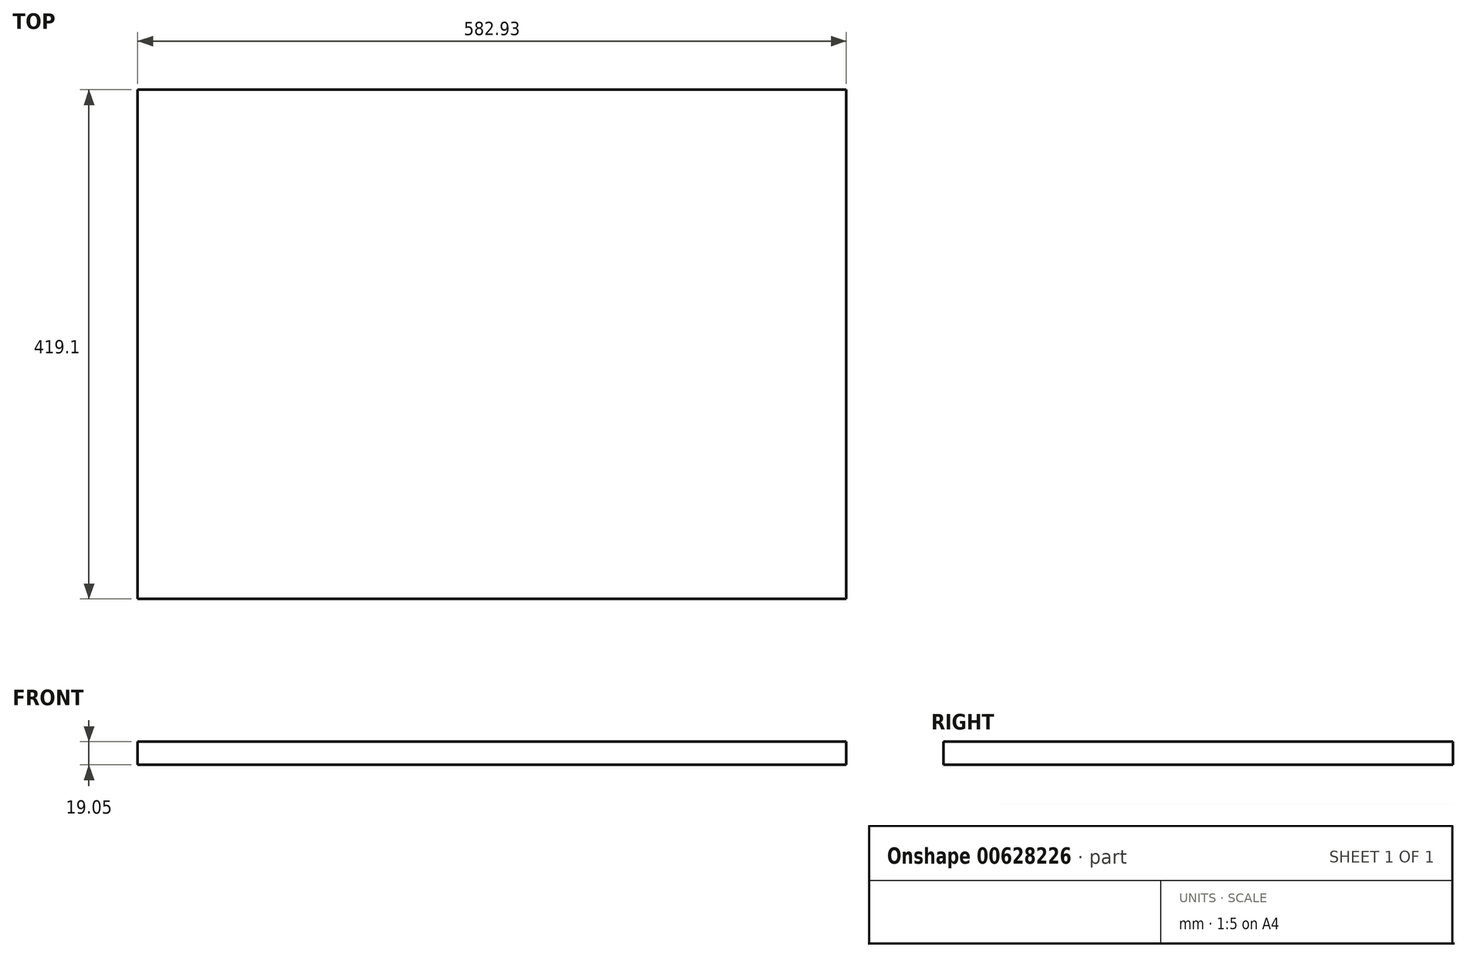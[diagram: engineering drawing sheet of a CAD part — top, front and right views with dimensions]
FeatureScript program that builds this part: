
annotation { "Feature Type Name" : "Feature", "Feature Type Description" : "" }
export const myFeature = defineFeature(function(context is Context, id is Id, definition is map)
    precondition{}
    {
        {
            var Q0;
            Q0=qCreatedBy(makeId("Top.planeOp"),FACE);
            var sketch = newSketch(context, id + "F0", { "sketchPlane" : qUnion([Q0])});
            skLineSegment(sketch, "E0.bottom", {"start": v(0, 0) * mm, "end": v(582.93, 0) * mm});
            skLineSegment(sketch, "E0.top", {"start": v(0, 419.1) * mm, "end": v(582.93, 419.1) * mm});
            skLineSegment(sketch, "E0.left", {"start": v(0, 0) * mm, "end": v(0, 419.1) * mm});
            skLineSegment(sketch, "E0.right", {"start": v(582.93, 0) * mm, "end": v(582.93, 419.1) * mm});
            skSolve(sketch);
        }
        {
            var Q0;
            Q0=makeQuery(id+"F0.imprint","IMPRINT",FACE,{"disambiguationData":[TD([[makeQuery(id+"F0.imprint","IMPRINT",EDGE,{"derivedFrom":sQuery(id+"F0.wireOp",EDGE,"E0.bottom")}),1.0]])]});
            extrude(context, id + "F1", {"entities" : qUnion([Q0]), "depth" : 19.05 * mm, "offsetDistance" : 25.4 * mm});
        }
    });
